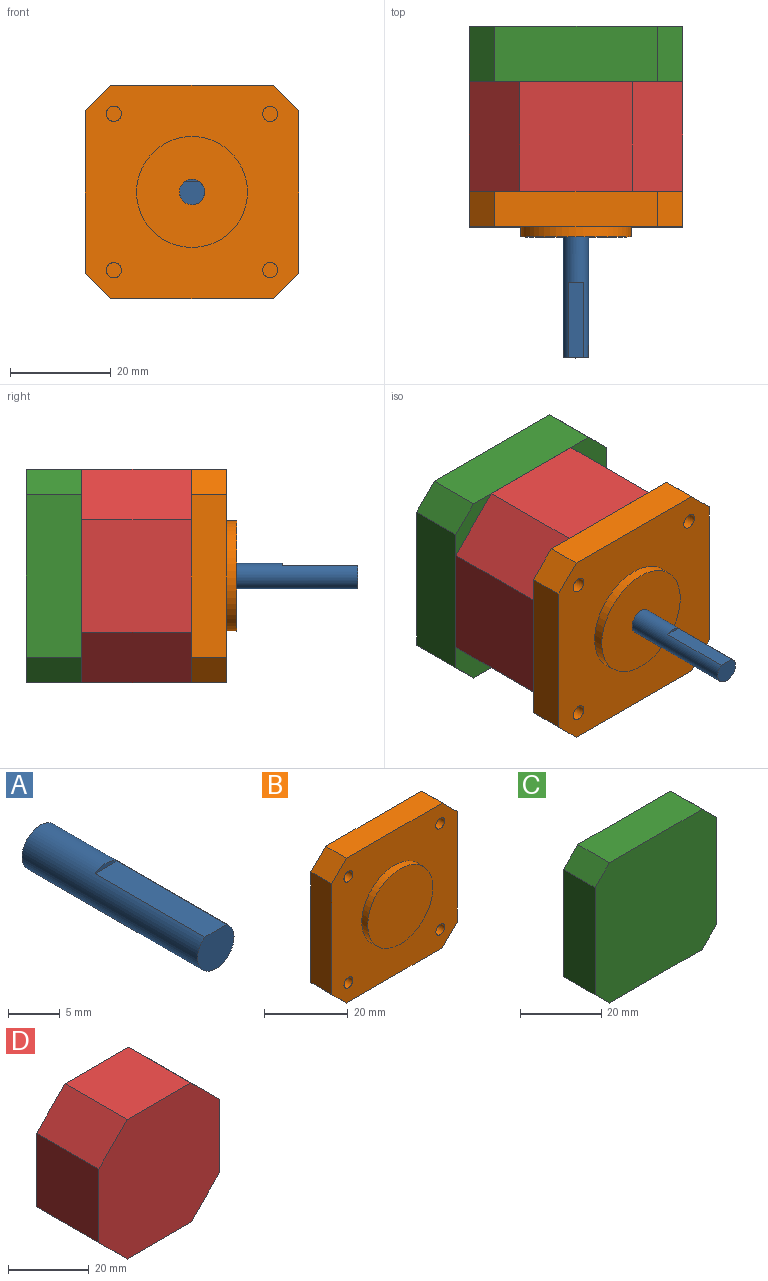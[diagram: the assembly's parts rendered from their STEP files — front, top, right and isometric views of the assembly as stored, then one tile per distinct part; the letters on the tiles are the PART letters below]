
ASSEMBLY  parts=4 mates=3
PART A: 5 faces, bbox 5x24x5 mm
  f0: cylinder r=2.5mm len=24mm, axis (0,1,0), area 328.7mm2, adj f1,f2,f3,f4
  f1: plane 5x4.5mm, normal (0,-1,0), area 18.6mm2, adj f0,f3
  f2: plane 5x5mm, normal (0,1,0), area 19.6mm2, adj f0
  f3: plane 15x3mm, normal (0,0,1), area 45mm2, adj f0,f1,f4
  f4: plane 3x0.5mm, normal (0,-1,0), area 1mm2, adj f0,f3
PART B: 20 faces, bbox 42.3x9x42.3 mm
  f0: plane 42.3x42.3mm, normal (0,-1,0), area 1330.9mm2, adj f1,f2,f3,f4,f6,f7,f8,f9
  f1: plane 32.3x7mm, normal (-1,0,0), area 226.1mm2, adj f0,f5,f6,f9
  f2: plane 32.3x7mm, normal (0,0,-1), area 226.1mm2, adj f0,f5,f6,f7
  f3: plane 32.3x7mm, normal (1,0,0), area 226.1mm2, adj f0,f5,f7,f8
  f4: plane 32.3x7mm, normal (0,0,1), area 226.1mm2, adj f0,f5,f8,f9
  f5: plane 42.3x42.3mm, normal (0,1,0), area 1739.3mm2, adj f1,f2,f3,f4,f6,f7,f8,f9
  f6: plane 7x5mm, normal (-0.71,0,-0.71), area 49.5mm2, adj f0,f1,f2,f5
  f7: plane 7x5mm, normal (0.71,0,-0.71), area 49.5mm2, adj f0,f2,f3,f5
  f8: plane 7x5mm, normal (0.71,0,0.71), area 49.5mm2, adj f0,f3,f4,f5
  f9: plane 7x5mm, normal (-0.71,0,0.71), area 49.5mm2, adj f0,f1,f4,f5
  f10: cylinder r=11mm len=22mm, axis (0,1,0), area 138.2mm2, adj f0,f11
  f11: plane 22x22mm, normal (0,-1,0), area 380.1mm2, adj f10
  f12: cylinder r=1.5mm len=4.5mm, axis (0,-1,0), area 42.4mm2, adj f0,f13
  f13: plane 3x3mm, normal (0,-1,0), area 7.1mm2, adj f12
  f14: cylinder r=1.5mm len=4.5mm, axis (0,-1,0), area 42.4mm2, adj f0,f15
  f15: plane 3x3mm, normal (0,-1,0), area 7.1mm2, adj f14
  f16: cylinder r=1.5mm len=4.5mm, axis (0,-1,0), area 42.4mm2, adj f0,f17
  f17: plane 3x3mm, normal (0,-1,0), area 7.1mm2, adj f16
  f18: cylinder r=1.5mm len=4.5mm, axis (0,-1,0), area 42.4mm2, adj f0,f19
  f19: plane 3x3mm, normal (0,-1,0), area 7.1mm2, adj f18
PART C: 18 faces, bbox 42.3x11x42.3 mm
  f0: plane 32.3x11mm, normal (1,0,0), area 355.3mm2, adj f4,f5,f8,f9
  f1: plane 32.3x11mm, normal (0,0,-1), area 355.3mm2, adj f4,f5,f7,f8
  f2: plane 32.3x11mm, normal (-1,0,0), area 355.3mm2, adj f4,f5,f6,f7
  f3: plane 32.3x11mm, normal (0,0,1), area 355.3mm2, adj f4,f5,f6,f9
  f4: plane 42.3x42.3mm, normal (0,1,0), area 1711mm2, adj f0,f1,f2,f3,f6,f7,f8,f9
  f5: plane 42.3x42.3mm, normal (0,-1,0), area 1739.3mm2, adj f0,f1,f2,f3,f6,f7,f8,f9
  f6: plane 11x5mm, normal (-0.71,0,0.71), area 77.8mm2, adj f2,f3,f4,f5
  f7: plane 11x5mm, normal (-0.71,0,-0.71), area 77.8mm2, adj f1,f2,f4,f5
  f8: plane 11x5mm, normal (0.71,0,-0.71), area 77.8mm2, adj f0,f1,f4,f5
  f9: plane 11x5mm, normal (0.71,0,0.71), area 77.8mm2, adj f0,f3,f4,f5
  f10: cylinder r=1.5mm len=4.5mm, axis (0,1,0), area 42.4mm2, adj f4,f11
  f11: plane 3x3mm, normal (0,1,0), area 7.1mm2, adj f10
  f12: cylinder r=1.5mm len=4.5mm, axis (0,1,0), area 42.4mm2, adj f4,f13
  f13: plane 3x3mm, normal (0,1,0), area 7.1mm2, adj f12
  f14: cylinder r=1.5mm len=4.5mm, axis (0,1,0), area 42.4mm2, adj f4,f15
  f15: plane 3x3mm, normal (0,1,0), area 7.1mm2, adj f14
  f16: cylinder r=1.5mm len=4.5mm, axis (0,1,0), area 42.4mm2, adj f4,f17
  f17: plane 3x3mm, normal (0,1,0), area 7.1mm2, adj f16
PART D: 10 faces, bbox 42.3x21.8x42.3 mm
  f0: plane 21.8x10mm, normal (0.71,0,0.71), area 308.3mm2, adj f3,f6,f7,f8
  f1: plane 21.8x10mm, normal (0.71,0,-0.71), area 308.3mm2, adj f3,f4,f6,f7
  f2: plane 21.8x10mm, normal (-0.71,0,0.71), area 308.3mm2, adj f6,f7,f8,f9
  f3: plane 22.3x21.8mm, normal (1,0,0), area 486.1mm2, adj f0,f1,f6,f7
  f4: plane 22.3x21.8mm, normal (0,0,-1), area 486.1mm2, adj f1,f5,f6,f7
  f5: plane 21.8x10mm, normal (-0.71,0,-0.71), area 308.3mm2, adj f4,f6,f7,f9
  f6: plane 42.3x42.3mm, normal (0,-1,0), area 1589.3mm2, adj f0,f1,f2,f3,f4,f5,f8,f9
  f7: plane 42.3x42.3mm, normal (0,1,0), area 1589.3mm2, adj f0,f1,f2,f3,f4,f5,f8,f9
  f8: plane 22.3x21.8mm, normal (0,0,1), area 486.1mm2, adj f0,f2,f6,f7
  f9: plane 22.3x21.8mm, normal (-1,0,0), area 486.1mm2, adj f2,f5,f6,f7
PLACE A t=(0.65,-30.39,153.81)mm
PLACE B rot(axis=(0,-1,0),90deg) t=(-4.37,-30.39,185.69)mm
PLACE C t=(0.65,-30.39,153.81)mm
PLACE D rot(axis=(0,-1,0),90deg) t=(-4.37,-30.39,185.69)mm
MATE fastened D.f7 <-> C.f5  axis (0,1,0) through (-17.8,-8.59,167.24)mm
MATE fastened B.f10 <-> D.f6  axis (0,1,0) through (-17.8,-30.39,167.24)mm
MATE fastened A.f0 <-> B.f10  axis (0,1,0) through (-17.8,-39.39,167.24)mm
